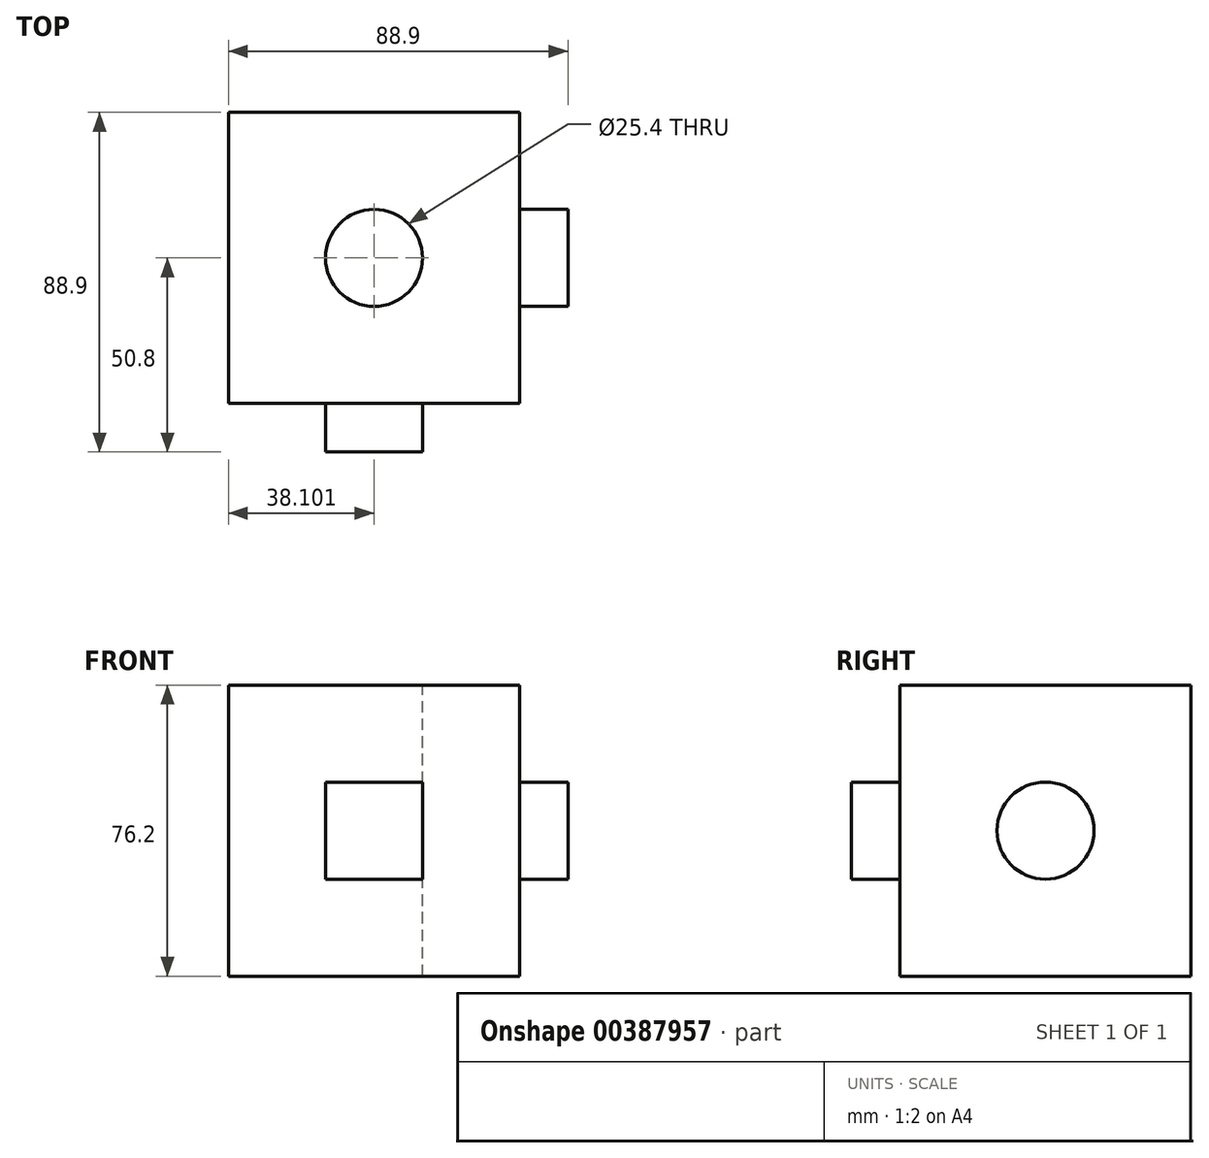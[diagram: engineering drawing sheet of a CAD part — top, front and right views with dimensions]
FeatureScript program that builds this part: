
annotation { "Feature Type Name" : "Feature", "Feature Type Description" : "" }
export const myFeature = defineFeature(function(context is Context, id is Id, definition is map)
    precondition{}
    {
        {
            var Q0;
            Q0=qCreatedBy(makeId("Front.planeOp"),FACE);
            var sketch = newSketch(context, id + "F0", { "sketchPlane" : qUnion([Q0])});
            skLineSegment(sketch, "E0.bottom", {"start": v(-38.67, 42.46) * mm, "end": v(37.53, 42.46) * mm});
            skLineSegment(sketch, "E0.top", {"start": v(-38.67, -33.74) * mm, "end": v(37.53, -33.74) * mm});
            skLineSegment(sketch, "E0.left", {"start": v(-38.67, 42.46) * mm, "end": v(-38.67, -33.74) * mm});
            skLineSegment(sketch, "E0.right", {"start": v(37.53, 42.46) * mm, "end": v(37.53, -33.74) * mm});
            skSolve(sketch);
        }
        {
            var Q0;
            Q0=makeQuery(id+"F0.imprint","IMPRINT",FACE,{"disambiguationData":[TD([[makeQuery(id+"F0.imprint","IMPRINT",EDGE,{"derivedFrom":sQuery(id+"F0.wireOp",EDGE,"E0.bottom")}),-1.0]])]});
            extrude(context, id + "F1", {"entities" : qUnion([Q0]), "depth" : 76.2 * mm});
        }
        {
            var Q0;
            Q0=makeQuery(id+"F1.opExtrude","SWEPT_FACE",FACE,{"disambiguationData":[OSD([sQuery(id+"F0.wireOp",EDGE,"E0.bottom")])]});
            var sketch = newSketch(context, id + "F2", { "sketchPlane" : qUnion([Q0])});
            skPoint(sketch, "E1", {"position": v(-0.57, -38.1) * mm});
            skSolve(sketch);
        }
        {
            var Q0;
            Q0=sQuery(id+"F2.wireOp",VERTEX,"E1");
            var Q1;
            Q1=makeQuery(id+"F1.opExtrude","SWEPT_BODY",BODY,{"disambiguationData":[OSD([sQuery(id+"F0.wireOp",EDGE,"E0.bottom"),sQuery(id+"F0.wireOp",EDGE,"E0.top"),sQuery(id+"F0.wireOp",EDGE,"E0.left"),sQuery(id+"F0.wireOp",EDGE,"E0.right")])]});
            hole(context, id + "F3", {"style" : HoleStyle.SIMPLE, "endStyle" : HoleEndStyle.THROUGH, "holeDiameter" : 25.4 * mm, "isTappedThrough" : true, "tappedDepth" : 12.7 * mm, "tapClearance" : 3, "locations" : qUnion([Q0]), "scope" : qUnion([Q1])});
        }
        {
            var Q0;
            Q0=makeQuery(id+"F1.opExtrude","CAP_FACE",FACE,{"disambiguationData":[OSD([sQuery(id+"F0.wireOp",EDGE,"E0.bottom"),sQuery(id+"F0.wireOp",EDGE,"E0.top"),sQuery(id+"F0.wireOp",EDGE,"E0.left"),sQuery(id+"F0.wireOp",EDGE,"E0.right")])],"isStart":false});
            var sketch = newSketch(context, id + "F4", { "sketchPlane" : qUnion([Q0])});
            skLineSegment(sketch, "E2.bottom", {"start": v(-13.27, 17.06) * mm, "end": v(12.13, 17.06) * mm});
            skLineSegment(sketch, "E2.top", {"start": v(-13.27, -8.34) * mm, "end": v(12.13, -8.34) * mm});
            skLineSegment(sketch, "E2.left", {"start": v(-13.27, 17.06) * mm, "end": v(-13.27, -8.34) * mm});
            skLineSegment(sketch, "E2.right", {"start": v(12.13, 17.06) * mm, "end": v(12.13, -8.34) * mm});
            skSolve(sketch);
        }
        {
            var Q0;
            Q0=makeQuery(id+"F4.imprint","IMPRINT",FACE,{"disambiguationData":[TD([[makeQuery(id+"F4.imprint","IMPRINT",EDGE,{"derivedFrom":sQuery(id+"F4.wireOp",EDGE,"E2.bottom")}),-1.0]])]});
            extrude(context, id + "F5", {"entities" : qUnion([Q0]), "operationType" : NewBodyOperationType.ADD, "depth" : 12.7 * mm});
        }
        {
            var Q0;
            Q0=makeQuery(id+"F1.opExtrude","SWEPT_FACE",FACE,{"disambiguationData":[OSD([sQuery(id+"F0.wireOp",EDGE,"E0.right")])]});
            var sketch = newSketch(context, id + "F6", { "sketchPlane" : qUnion([Q0])});
            skCircle(sketch, "E3", {"center": v(-38.1, 4.36) * mm, "radius": 12.7 * mm});
            skSolve(sketch);
        }
        {
            var Q0;
            Q0=makeQuery(id+"F6.imprint","IMPRINT",FACE,{"disambiguationData":[TD([[makeQuery(id+"F6.imprint","IMPRINT",EDGE,{"derivedFrom":sQuery(id+"F6.wireOp",EDGE,"E3")}),1.0]])]});
            extrude(context, id + "F7", {"entities" : qUnion([Q0]), "operationType" : NewBodyOperationType.ADD, "depth" : 12.7 * mm});
        }
    });
